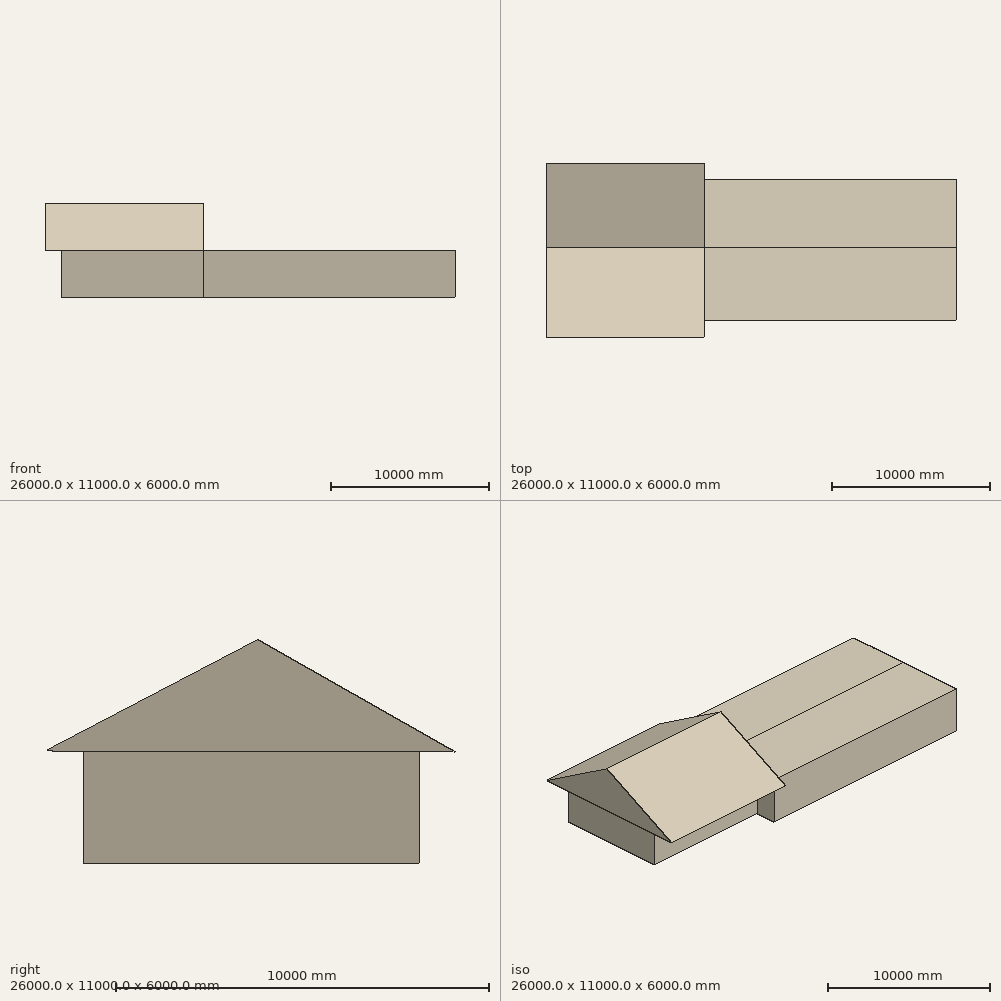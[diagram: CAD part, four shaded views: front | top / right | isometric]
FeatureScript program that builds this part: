
annotation { "Feature Type Name" : "Feature", "Feature Type Description" : "" }
export const myFeature = defineFeature(function(context is Context, id is Id, definition is map)
    precondition{}
    {
        {
            var Q0;
            Q0=qCreatedBy(makeId("Right.planeOp"),FACE);
            var sketch = newSketch(context, id + "F0", { "sketchPlane" : qUnion([Q0])});
            skLineSegment(sketch, "E0.bottom", {"start": v(-73.35, 2968.74) * mm, "end": v(8926.65, 2968.74) * mm});
            skLineSegment(sketch, "E0.top", {"start": v(-73.35, -31.26) * mm, "end": v(8926.65, -31.26) * mm});
            skLineSegment(sketch, "E0.left", {"start": v(-73.35, 2968.74) * mm, "end": v(-73.35, -31.26) * mm});
            skLineSegment(sketch, "E0.right", {"start": v(8926.65, 2968.74) * mm, "end": v(8926.65, -31.26) * mm});
            skLineSegment(sketch, "E1", {"start": v(-1105.9, 2982.91) * mm, "end": v(4593.08, 5968.76) * mm});
            skLineSegment(sketch, "E2", {"start": v(4593.08, 5968.76) * mm, "end": v(9894.07, 2955.58) * mm});
            skLineSegment(sketch, "E3", {"start": v(9894.07, 2955.58) * mm, "end": v(-1105.9, 2982.91) * mm});
            skSolve(sketch);
        }
        {
            var Q0;
            {var subQ1=sQuery(id+"F0.wireOp",EDGE,"E0.top");Q0=makeQuery(id+"F0.imprint","IMPRINT",FACE,{"disambiguationData":[TD([[makeQuery(id+"F0.imprint","IMPRINT",EDGE,{"derivedFrom":subQ1}),1.0]])]});}
            extrude(context, id + "F1", {"entities" : qUnion([Q0]), "depth" : 16000 * mm});
        }
        {
            var Q0;
            Q0=makeQuery(id+"F1.opExtrude","CAP_FACE",FACE,{"disambiguationData":[OSD([sQuery(id+"F0.wireOp",EDGE,"E0.bottom"),sQuery(id+"F0.wireOp",EDGE,"E0.top"),sQuery(id+"F0.wireOp",EDGE,"E0.left"),sQuery(id+"F0.wireOp",EDGE,"E0.right"),sQuery(id+"F0.wireOp",EDGE,"E3")])],"isStart":true});
            var sketch = newSketch(context, id + "F2", { "sketchPlane" : qUnion([Q0])});
            skLineSegment(sketch, "E4.bottom", {"start": v(-8926.65, -31.26) * mm, "end": v(-1426.65, -31.26) * mm});
            skLineSegment(sketch, "E4.top", {"start": v(-8926.65, 2968.74) * mm, "end": v(-1426.65, 2968.74) * mm});
            skLineSegment(sketch, "E4.left", {"start": v(-8926.65, -31.26) * mm, "end": v(-8926.65, 2968.74) * mm});
            skLineSegment(sketch, "E4.right", {"start": v(-1426.65, -31.26) * mm, "end": v(-1426.65, 2968.74) * mm});
            skSolve(sketch);
        }
        {
            var Q0;
            Q0 = qSketchRegion(id + "F2", true);
            extrude(context, id + "F3", {"entities" : qUnion([Q0]), "operationType" : NewBodyOperationType.ADD, "depth" : 9000 * mm});
        }
        {
            var Q0;
            Q0=sQuery(id+"F0.wireOp",EDGE,"E2");
            var Q1;
            Q1=sQuery(id+"F0.wireOp",EDGE,"E1");
            extrude(context, id + "F4", {"bodyType" : ToolBodyType.SURFACE, "surfaceEntities" : qUnion([Q0, Q1]), "depth" : 16000 * mm});
        }
        {
            var Q0;
            {var subQ6=sQuery(id+"F0.wireOp",EDGE,"E1");Q0=makeQuery(id+"F0.imprint","IMPRINT",FACE,{"disambiguationData":[TD([[makeQuery(id+"F0.imprint","IMPRINT",EDGE,{"derivedFrom":subQ6}),-1.0]])]});}
            extrude(context, id + "F5", {"entities" : qUnion([Q0]), "operationType" : NewBodyOperationType.ADD, "oppositeDirection" : true, "depth" : 10000 * mm});
        }
    });
